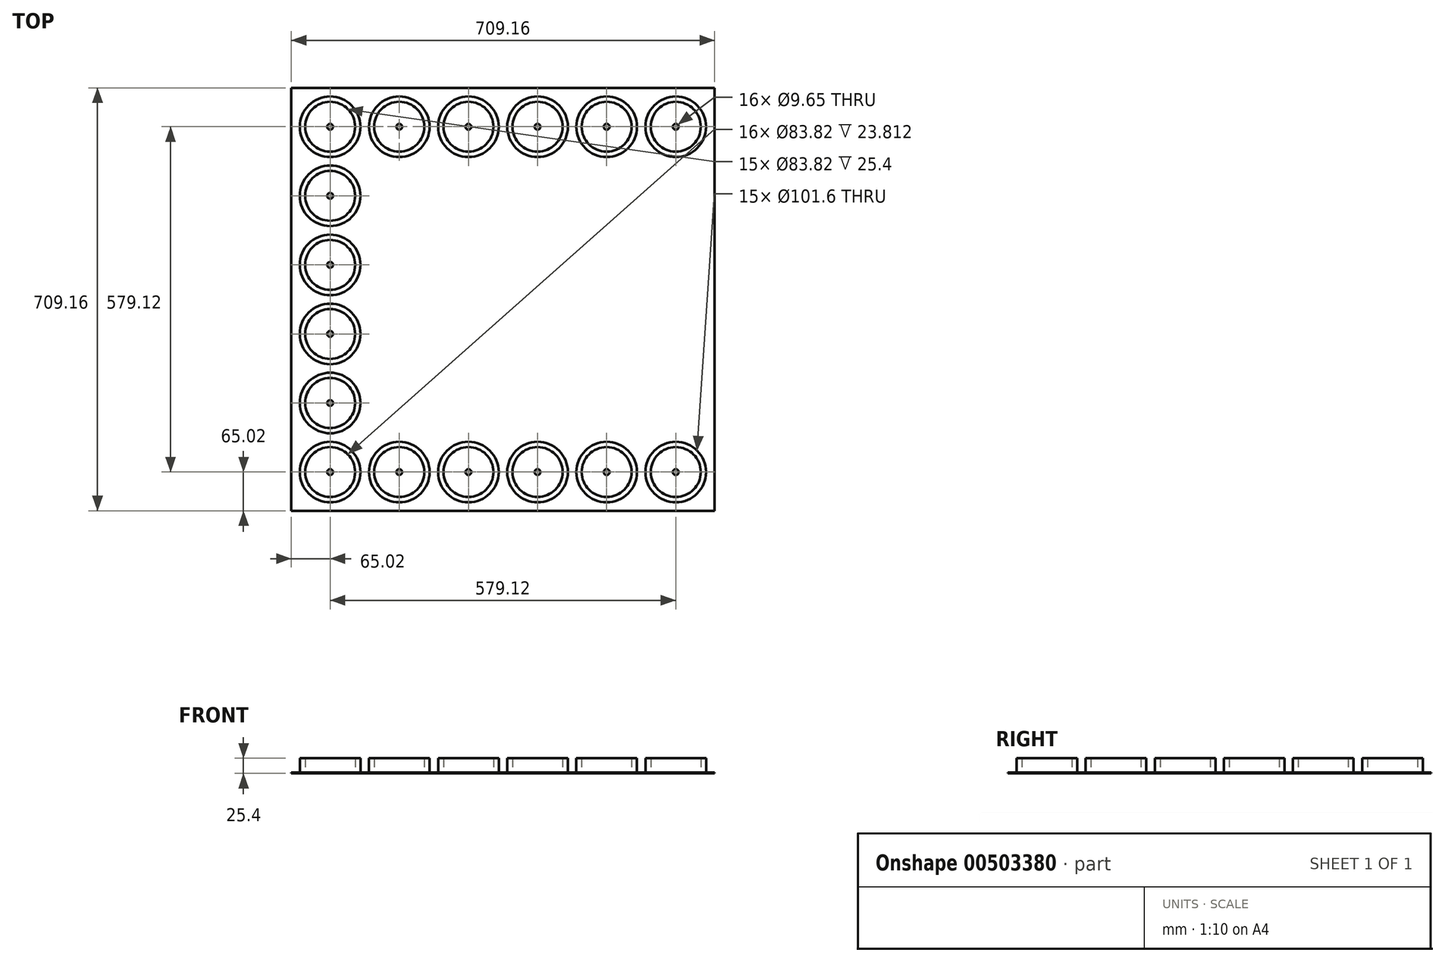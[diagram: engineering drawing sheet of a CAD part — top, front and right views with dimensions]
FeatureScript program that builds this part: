
annotation { "Feature Type Name" : "Feature", "Feature Type Description" : "" }
export const myFeature = defineFeature(function(context is Context, id is Id, definition is map)
    precondition{}
    {
        {
            var Q0;
            Q0=qCreatedBy(makeId("Top.planeOp"),FACE);
            var sketch = newSketch(context, id + "F0", { "sketchPlane" : qUnion([Q0])});
            skLineSegment(sketch, "E0.bottom", {"start": v(354.58, 354.58) * mm, "end": v(-354.58, 354.58) * mm});
            skLineSegment(sketch, "E0.top", {"start": v(354.58, -354.58) * mm, "end": v(-354.58, -354.58) * mm});
            skLineSegment(sketch, "E0.left", {"start": v(354.58, 354.58) * mm, "end": v(354.58, -354.58) * mm});
            skLineSegment(sketch, "E0.right", {"start": v(-354.58, 354.58) * mm, "end": v(-354.58, -354.58) * mm});
            skPoint(sketch, "E0.middle", {"position": v(0, 0) * mm});
            skCircle(sketch, "E1", {"center": v(289.56, -289.56) * mm, "radius": 4.83 * mm});
            skCircle(sketch, "E2", {"center": v(289.56, -289.56) * mm, "radius": 41.91 * mm});
            skCircle(sketch, "E3", {"center": v(173.74, -289.56) * mm, "radius": 41.91 * mm});
            skCircle(sketch, "E4", {"center": v(57.91, -289.56) * mm, "radius": 41.91 * mm});
            skCircle(sketch, "E5", {"center": v(-57.91, -289.56) * mm, "radius": 4.83 * mm});
            skCircle(sketch, "E6", {"center": v(-57.91, -289.56) * mm, "radius": 41.91 * mm});
            skCircle(sketch, "E7", {"center": v(-173.74, -289.56) * mm, "radius": 41.91 * mm});
            skCircle(sketch, "E8", {"center": v(-289.56, -289.56) * mm, "radius": 41.91 * mm});
            skCircle(sketch, "E9", {"center": v(173.74, -289.56) * mm, "radius": 4.83 * mm});
            skCircle(sketch, "E10", {"center": v(57.91, -289.56) * mm, "radius": 4.83 * mm});
            skCircle(sketch, "E11", {"center": v(-173.74, -289.56) * mm, "radius": 4.83 * mm});
            skCircle(sketch, "E12", {"center": v(-289.56, -289.56) * mm, "radius": 4.83 * mm});
            skCircle(sketch, "E13", {"center": v(-289.56, -289.56) * mm, "radius": 50.8 * mm});
            skCircle(sketch, "E14", {"center": v(-173.74, -289.56) * mm, "radius": 50.8 * mm});
            skCircle(sketch, "E15", {"center": v(-57.91, -289.56) * mm, "radius": 50.8 * mm});
            skCircle(sketch, "E16", {"center": v(57.91, -289.56) * mm, "radius": 50.8 * mm});
            skCircle(sketch, "E17", {"center": v(173.74, -289.56) * mm, "radius": 50.8 * mm});
            skCircle(sketch, "E18", {"center": v(289.56, -289.56) * mm, "radius": 50.8 * mm});
            skCircle(sketch, "E19", {"center": v(-289.56, -173.74) * mm, "radius": 41.91 * mm});
            skCircle(sketch, "E20", {"center": v(-289.56, -173.74) * mm, "radius": 4.83 * mm});
            skCircle(sketch, "E21", {"center": v(-289.56, -173.74) * mm, "radius": 50.8 * mm});
            skCircle(sketch, "E22", {"center": v(-289.56, -57.91) * mm, "radius": 41.91 * mm});
            skCircle(sketch, "E23", {"center": v(-289.56, -57.91) * mm, "radius": 4.83 * mm});
            skCircle(sketch, "E24", {"center": v(-289.56, -57.91) * mm, "radius": 50.8 * mm});
            skCircle(sketch, "E25", {"center": v(-289.56, 57.91) * mm, "radius": 41.91 * mm});
            skCircle(sketch, "E26", {"center": v(-289.56, 57.91) * mm, "radius": 4.83 * mm});
            skCircle(sketch, "E27", {"center": v(-289.56, 57.91) * mm, "radius": 50.8 * mm});
            skCircle(sketch, "E28", {"center": v(-289.56, 173.74) * mm, "radius": 41.91 * mm});
            skCircle(sketch, "E29", {"center": v(-289.56, 173.74) * mm, "radius": 4.83 * mm});
            skCircle(sketch, "E30", {"center": v(-289.56, 173.74) * mm, "radius": 50.8 * mm});
            skCircle(sketch, "E31", {"center": v(-289.56, 289.56) * mm, "radius": 41.91 * mm});
            skCircle(sketch, "E32", {"center": v(-289.56, 289.56) * mm, "radius": 4.83 * mm});
            skCircle(sketch, "E33", {"center": v(-289.56, 289.56) * mm, "radius": 50.8 * mm});
            skCircle(sketch, "E34", {"center": v(289.56, 289.56) * mm, "radius": 4.83 * mm});
            skCircle(sketch, "E35", {"center": v(289.56, 289.56) * mm, "radius": 41.91 * mm});
            skCircle(sketch, "E36", {"center": v(173.74, 289.56) * mm, "radius": 41.91 * mm});
            skCircle(sketch, "E37", {"center": v(57.91, 289.56) * mm, "radius": 41.91 * mm});
            skCircle(sketch, "E38", {"center": v(-57.91, 289.56) * mm, "radius": 4.83 * mm});
            skCircle(sketch, "E39", {"center": v(-57.91, 289.56) * mm, "radius": 41.91 * mm});
            skCircle(sketch, "E40", {"center": v(-173.74, 289.56) * mm, "radius": 41.91 * mm});
            skCircle(sketch, "E41", {"center": v(173.74, 289.56) * mm, "radius": 4.83 * mm});
            skCircle(sketch, "E42", {"center": v(57.91, 289.56) * mm, "radius": 4.83 * mm});
            skCircle(sketch, "E43", {"center": v(-173.74, 289.56) * mm, "radius": 4.83 * mm});
            skCircle(sketch, "E44", {"center": v(-173.74, 289.56) * mm, "radius": 50.8 * mm});
            skCircle(sketch, "E45", {"center": v(-57.91, 289.56) * mm, "radius": 50.8 * mm});
            skCircle(sketch, "E46", {"center": v(57.91, 289.56) * mm, "radius": 50.8 * mm});
            skCircle(sketch, "E47", {"center": v(173.74, 289.56) * mm, "radius": 50.8 * mm});
            skCircle(sketch, "E48", {"center": v(289.56, 289.56) * mm, "radius": 50.8 * mm});
            skSolve(sketch);
        }
        {
            var Q0;
            Q0 = qSketchRegion(id + "F0", true);
            extrude(context, id + "F1", {"entities" : qUnion([Q0]), "depth" : 1.59 * mm});
        }
        {
            var Q0;
            Q0=makeQuery(id+"F0.imprint","IMPRINT",FACE,{"disambiguationData":[TD([[makeQuery(id+"F0.imprint","IMPRINT",EDGE,{"derivedFrom":sQuery(id+"F0.wireOp",EDGE,"E40")}),-1.0]])]});
            extrude(context, id + "F2", {"entities" : qUnion([Q0]), "operationType" : NewBodyOperationType.ADD, "depth" : 25.4 * mm});
        }
        {
            var Q0;
            Q0=makeQuery(id+"F0.imprint","IMPRINT",FACE,{"disambiguationData":[TD([[makeQuery(id+"F0.imprint","IMPRINT",EDGE,{"derivedFrom":sQuery(id+"F0.wireOp",EDGE,"E31")}),1.0]])]});
            var Q1;
            Q1=makeQuery(id+"F0.imprint","IMPRINT",FACE,{"disambiguationData":[TD([[makeQuery(id+"F0.imprint","IMPRINT",EDGE,{"derivedFrom":sQuery(id+"F0.wireOp",EDGE,"E40")}),1.0]])]});
            var Q2;
            Q2=makeQuery(id+"F0.imprint","IMPRINT",FACE,{"disambiguationData":[TD([[makeQuery(id+"F0.imprint","IMPRINT",EDGE,{"derivedFrom":sQuery(id+"F0.wireOp",EDGE,"E38")}),-1.0]])]});
            var Q3;
            Q3=makeQuery(id+"F0.imprint","IMPRINT",FACE,{"disambiguationData":[TD([[makeQuery(id+"F0.imprint","IMPRINT",EDGE,{"derivedFrom":sQuery(id+"F0.wireOp",EDGE,"E37")}),1.0]])]});
            var Q4;
            Q4=makeQuery(id+"F0.imprint","IMPRINT",FACE,{"disambiguationData":[TD([[makeQuery(id+"F0.imprint","IMPRINT",EDGE,{"derivedFrom":sQuery(id+"F0.wireOp",EDGE,"E36")}),1.0]])]});
            var Q5;
            Q5=makeQuery(id+"F0.imprint","IMPRINT",FACE,{"disambiguationData":[TD([[makeQuery(id+"F0.imprint","IMPRINT",EDGE,{"derivedFrom":sQuery(id+"F0.wireOp",EDGE,"E28")}),1.0]])]});
            var Q6;
            Q6=makeQuery(id+"F0.imprint","IMPRINT",FACE,{"disambiguationData":[TD([[makeQuery(id+"F0.imprint","IMPRINT",EDGE,{"derivedFrom":sQuery(id+"F0.wireOp",EDGE,"E25")}),1.0]])]});
            var Q7;
            Q7=makeQuery(id+"F0.imprint","IMPRINT",FACE,{"disambiguationData":[TD([[makeQuery(id+"F0.imprint","IMPRINT",EDGE,{"derivedFrom":sQuery(id+"F0.wireOp",EDGE,"E22")}),1.0]])]});
            var Q8;
            Q8=makeQuery(id+"F0.imprint","IMPRINT",FACE,{"disambiguationData":[TD([[makeQuery(id+"F0.imprint","IMPRINT",EDGE,{"derivedFrom":sQuery(id+"F0.wireOp",EDGE,"E19")}),1.0]])]});
            var Q9;
            Q9=makeQuery(id+"F0.imprint","IMPRINT",FACE,{"disambiguationData":[TD([[makeQuery(id+"F0.imprint","IMPRINT",EDGE,{"derivedFrom":sQuery(id+"F0.wireOp",EDGE,"E7")}),1.0]])]});
            var Q10;
            Q10=makeQuery(id+"F0.imprint","IMPRINT",FACE,{"disambiguationData":[TD([[makeQuery(id+"F0.imprint","IMPRINT",EDGE,{"derivedFrom":sQuery(id+"F0.wireOp",EDGE,"E8")}),1.0]])]});
            var Q11;
            Q11=makeQuery(id+"F0.imprint","IMPRINT",FACE,{"disambiguationData":[TD([[makeQuery(id+"F0.imprint","IMPRINT",EDGE,{"derivedFrom":sQuery(id+"F0.wireOp",EDGE,"E5")}),-1.0]])]});
            var Q12;
            Q12=makeQuery(id+"F0.imprint","IMPRINT",FACE,{"disambiguationData":[TD([[makeQuery(id+"F0.imprint","IMPRINT",EDGE,{"derivedFrom":sQuery(id+"F0.wireOp",EDGE,"E4")}),1.0]])]});
            var Q13;
            Q13=makeQuery(id+"F0.imprint","IMPRINT",FACE,{"disambiguationData":[TD([[makeQuery(id+"F0.imprint","IMPRINT",EDGE,{"derivedFrom":sQuery(id+"F0.wireOp",EDGE,"E3")}),1.0]])]});
            var Q14;
            Q14=makeQuery(id+"F0.imprint","IMPRINT",FACE,{"disambiguationData":[TD([[makeQuery(id+"F0.imprint","IMPRINT",EDGE,{"derivedFrom":sQuery(id+"F0.wireOp",EDGE,"E1")}),-1.0]])]});
            var Q15;
            Q15=makeQuery(id+"F0.imprint","IMPRINT",FACE,{"disambiguationData":[TD([[makeQuery(id+"F0.imprint","IMPRINT",EDGE,{"derivedFrom":sQuery(id+"F0.wireOp",EDGE,"E34")}),-1.0]])]});
            extrude(context, id + "F3", {"entities" : qUnion([Q0, Q1, Q2, Q3, Q4, Q5, Q6, Q7, Q8, Q9, Q10, Q11, Q12, Q13, Q14, Q15]), "operationType" : NewBodyOperationType.ADD, "depth" : 1.59 * mm});
        }
        {
            var Q0;
            Q0=makeQuery(id+"F0.imprint","IMPRINT",FACE,{"disambiguationData":[TD([[makeQuery(id+"F0.imprint","IMPRINT",EDGE,{"derivedFrom":sQuery(id+"F0.wireOp",EDGE,"E31")}),-1.0]])]});
            var Q1;
            Q1=makeQuery(id+"F0.imprint","IMPRINT",FACE,{"disambiguationData":[TD([[makeQuery(id+"F0.imprint","IMPRINT",EDGE,{"derivedFrom":sQuery(id+"F0.wireOp",EDGE,"E39")}),-1.0]])]});
            var Q2;
            Q2=makeQuery(id+"F0.imprint","IMPRINT",FACE,{"disambiguationData":[TD([[makeQuery(id+"F0.imprint","IMPRINT",EDGE,{"derivedFrom":sQuery(id+"F0.wireOp",EDGE,"E37")}),-1.0]])]});
            var Q3;
            Q3=makeQuery(id+"F0.imprint","IMPRINT",FACE,{"disambiguationData":[TD([[makeQuery(id+"F0.imprint","IMPRINT",EDGE,{"derivedFrom":sQuery(id+"F0.wireOp",EDGE,"E28")}),-1.0]])]});
            var Q4;
            Q4=makeQuery(id+"F0.imprint","IMPRINT",FACE,{"disambiguationData":[TD([[makeQuery(id+"F0.imprint","IMPRINT",EDGE,{"derivedFrom":sQuery(id+"F0.wireOp",EDGE,"E25")}),-1.0]])]});
            var Q5;
            Q5=makeQuery(id+"F0.imprint","IMPRINT",FACE,{"disambiguationData":[TD([[makeQuery(id+"F0.imprint","IMPRINT",EDGE,{"derivedFrom":sQuery(id+"F0.wireOp",EDGE,"E22")}),-1.0]])]});
            var Q6;
            Q6=makeQuery(id+"F0.imprint","IMPRINT",FACE,{"disambiguationData":[TD([[makeQuery(id+"F0.imprint","IMPRINT",EDGE,{"derivedFrom":sQuery(id+"F0.wireOp",EDGE,"E36")}),-1.0]])]});
            var Q7;
            Q7=makeQuery(id+"F0.imprint","IMPRINT",FACE,{"disambiguationData":[TD([[makeQuery(id+"F0.imprint","IMPRINT",EDGE,{"derivedFrom":sQuery(id+"F0.wireOp",EDGE,"E35")}),-1.0]])]});
            var Q8;
            Q8=makeQuery(id+"F0.imprint","IMPRINT",FACE,{"disambiguationData":[TD([[makeQuery(id+"F0.imprint","IMPRINT",EDGE,{"derivedFrom":sQuery(id+"F0.wireOp",EDGE,"E19")}),-1.0]])]});
            var Q9;
            Q9=makeQuery(id+"F0.imprint","IMPRINT",FACE,{"disambiguationData":[TD([[makeQuery(id+"F0.imprint","IMPRINT",EDGE,{"derivedFrom":sQuery(id+"F0.wireOp",EDGE,"E8")}),-1.0]])]});
            var Q10;
            Q10=makeQuery(id+"F0.imprint","IMPRINT",FACE,{"disambiguationData":[TD([[makeQuery(id+"F0.imprint","IMPRINT",EDGE,{"derivedFrom":sQuery(id+"F0.wireOp",EDGE,"E7")}),-1.0]])]});
            var Q11;
            Q11=makeQuery(id+"F0.imprint","IMPRINT",FACE,{"disambiguationData":[TD([[makeQuery(id+"F0.imprint","IMPRINT",EDGE,{"derivedFrom":sQuery(id+"F0.wireOp",EDGE,"E6")}),-1.0]])]});
            var Q12;
            Q12=makeQuery(id+"F0.imprint","IMPRINT",FACE,{"disambiguationData":[TD([[makeQuery(id+"F0.imprint","IMPRINT",EDGE,{"derivedFrom":sQuery(id+"F0.wireOp",EDGE,"E4")}),-1.0]])]});
            var Q13;
            Q13=makeQuery(id+"F0.imprint","IMPRINT",FACE,{"disambiguationData":[TD([[makeQuery(id+"F0.imprint","IMPRINT",EDGE,{"derivedFrom":sQuery(id+"F0.wireOp",EDGE,"E3")}),-1.0]])]});
            var Q14;
            Q14=makeQuery(id+"F0.imprint","IMPRINT",FACE,{"disambiguationData":[TD([[makeQuery(id+"F0.imprint","IMPRINT",EDGE,{"derivedFrom":sQuery(id+"F0.wireOp",EDGE,"E2")}),-1.0]])]});
            extrude(context, id + "F4", {"entities" : qUnion([Q0, Q1, Q2, Q3, Q4, Q5, Q6, Q7, Q8, Q9, Q10, Q11, Q12, Q13, Q14]), "depth" : 25.4 * mm});
        }
    });
